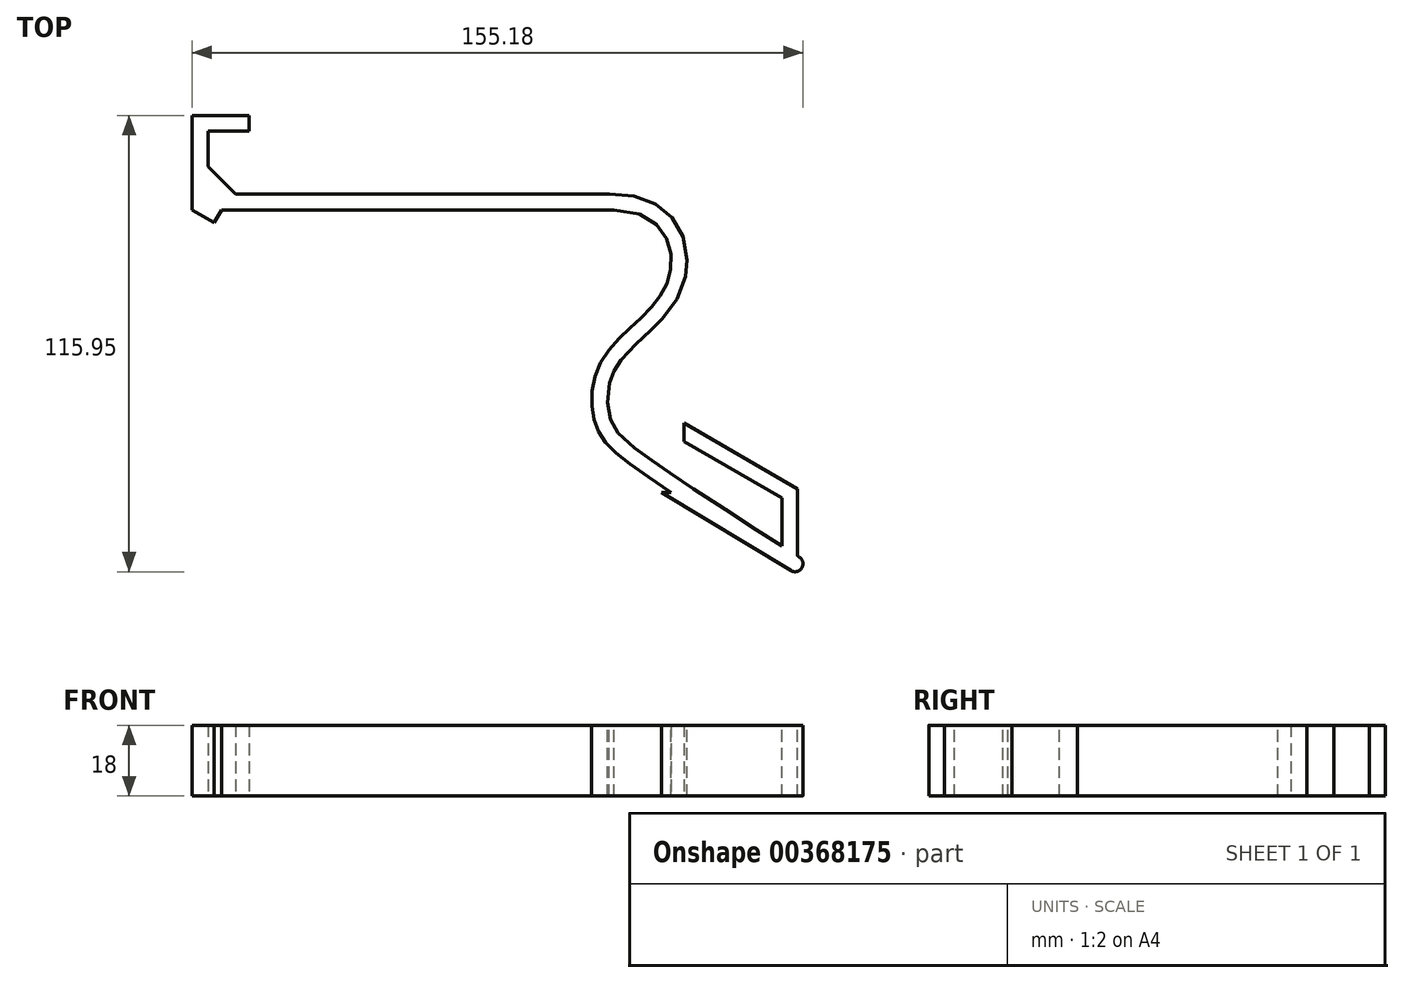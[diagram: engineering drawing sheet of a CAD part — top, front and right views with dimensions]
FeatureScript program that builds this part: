
annotation { "Feature Type Name" : "Feature", "Feature Type Description" : "" }
export const myFeature = defineFeature(function(context is Context, id is Id, definition is map)
    precondition{}
    {
        {
            var Q0;
            Q0=qCreatedBy(makeId("Top.planeOp"),FACE);
            var sketch = newSketch(context, id + "F0", { "sketchPlane" : qUnion([Q0])});
            skLineSegment(sketch, "E0", {"start": v(0, 16) * mm, "end": v(-10.43, 16) * mm});
            skLineSegment(sketch, "E1", {"start": v(-10.43, 16) * mm, "end": v(-10.43, 0) * mm});
            skLineSegment(sketch, "E2", {"start": v(-10.43, 0) * mm, "end": v(95.57, 0) * mm});
            skLineSegment(sketch, "E3.0", {"start": v(-14.43, -4) * mm, "end": v(95.57, -4) * mm});
            skLineSegment(sketch, "E3.1", {"start": v(-14.43, 20) * mm, "end": v(-14.43, -4) * mm});
            skLineSegment(sketch, "E3.2", {"start": v(0, 20) * mm, "end": v(-14.43, 20) * mm});
            skLineSegment(sketch, "E4", {"start": v(0, 16) * mm, "end": v(0, 20) * mm});
            skLineSegment(sketch, "E5", {"start": v(95.57, 0) * mm, "end": v(95.57, -4) * mm});
            skLineSegment(sketch, "E6", {"start": v(-10.43, 7) * mm, "end": v(-3.43, 0) * mm});
            skLineSegment(sketch, "E7", {"start": v(95.57, -4) * mm, "end": v(95.57, -70.27) * mm});
            skLineSegment(sketch, "E8", {"start": v(95.57, -70.27) * mm, "end": v(91.57, -67.86) * mm});
            skLineSegment(sketch, "E9", {"start": v(91.57, -67.86) * mm, "end": v(91.57, -4) * mm});
            skLineSegment(sketch, "E10", {"start": v(-14.43, -4) * mm, "end": v(95.57, -70.27) * mm, "construction": true});
            skSolve(sketch);
        }
        {
            var Q0;
            Q0=qSketchRegion(id+"F0",true);
            extrude(context, id + "F1", {"entities" : qUnion([Q0]), "depth" : 18 * mm, "symmetric" : true});
        }
        {
            var Q0;
            Q0=makeQuery(id+"F1.opExtrude","CAP_FACE",FACE,{"disambiguationData":[OSD([sQuery(id+"F0.wireOp",EDGE,"E0"),sQuery(id+"F0.wireOp",EDGE,"E1"),sQuery(id+"F0.wireOp",EDGE,"E2"),sQuery(id+"F0.wireOp",EDGE,"E3.0"),sQuery(id+"F0.wireOp",EDGE,"E3.1"),sQuery(id+"F0.wireOp",EDGE,"E3.2"),sQuery(id+"F0.wireOp",EDGE,"E4"),sQuery(id+"F0.wireOp",EDGE,"E5"),sQuery(id+"F0.wireOp",EDGE,"E6"),sQuery(id+"F0.wireOp",EDGE,"E7"),sQuery(id+"F0.wireOp",EDGE,"E8"),sQuery(id+"F0.wireOp",EDGE,"E9")])],"isStart":false});
            var sketch = newSketch(context, id + "F2", { "sketchPlane" : qUnion([Q0])});
            skLineSegment(sketch, "E11", {"start": v(95.57, -70.27) * mm, "end": v(-14.43, -4) * mm});
            skLineSegment(sketch, "E12", {"start": v(-14.43, -4) * mm, "end": v(-43.04, -4) * mm});
            skLineSegment(sketch, "E13", {"start": v(-43.04, -4) * mm, "end": v(-43.04, -70.27) * mm});
            skLineSegment(sketch, "E14", {"start": v(-43.04, -70.27) * mm, "end": v(95.57, -70.27) * mm});
            skSolve(sketch);
        }
        {
            var Q0;
            Q0=qSketchRegion(id+"F2",true);
            extrude(context, id + "F3", {"entities" : qUnion([Q0]), "operationType" : NewBodyOperationType.REMOVE, "oppositeDirection" : true, "depth" : 25 * mm});
        }
        {
            var Q0;
            Q0=makeQuery(id+"F1.opExtrude","CAP_FACE",FACE,{"disambiguationData":[OSD([sQuery(id+"F0.wireOp",EDGE,"E0"),sQuery(id+"F0.wireOp",EDGE,"E1"),sQuery(id+"F0.wireOp",EDGE,"E2"),sQuery(id+"F0.wireOp",EDGE,"E3.0"),sQuery(id+"F0.wireOp",EDGE,"E3.1"),sQuery(id+"F0.wireOp",EDGE,"E3.2"),sQuery(id+"F0.wireOp",EDGE,"E4"),sQuery(id+"F0.wireOp",EDGE,"E5"),sQuery(id+"F0.wireOp",EDGE,"E6"),sQuery(id+"F0.wireOp",EDGE,"E7"),sQuery(id+"F0.wireOp",EDGE,"E8"),sQuery(id+"F0.wireOp",EDGE,"E9")])],"isStart":false});
            var sketch = newSketch(context, id + "F4", { "sketchPlane" : qUnion([Q0])});
            skCircle(sketch, "E15.cCircle", {"center": v(91.57, -4) * mm, "radius": 63.86 * mm, "construction": true});
            skLineSegment(sketch, "E15.0", {"start": v(91.57, -67.86) * mm, "end": v(36.26, -35.93) * mm});
            skLineSegment(sketch, "E15.1", {"start": v(36.26, -35.93) * mm, "end": v(36.26, 27.93) * mm});
            skLineSegment(sketch, "E15.2", {"start": v(36.26, 27.93) * mm, "end": v(91.57, 59.86) * mm});
            skLineSegment(sketch, "E15.3", {"start": v(91.57, 59.86) * mm, "end": v(146.87, 27.93) * mm});
            skLineSegment(sketch, "E15.4", {"start": v(146.87, 27.93) * mm, "end": v(146.87, -35.93) * mm});
            skLineSegment(sketch, "E15.5", {"start": v(146.87, -35.93) * mm, "end": v(91.57, -67.86) * mm});
            skCircle(sketch, "E16.cCircle", {"center": v(91.57, -4) * mm, "radius": 59.86 * mm, "construction": true});
            skLineSegment(sketch, "E16.0", {"start": v(91.57, -63.86) * mm, "end": v(39.73, -33.93) * mm});
            skLineSegment(sketch, "E16.1", {"start": v(39.73, -33.93) * mm, "end": v(39.73, 25.93) * mm});
            skLineSegment(sketch, "E16.2", {"start": v(39.73, 25.93) * mm, "end": v(91.57, 55.86) * mm});
            skLineSegment(sketch, "E16.3", {"start": v(91.57, 55.86) * mm, "end": v(143.4, 25.93) * mm});
            skLineSegment(sketch, "E16.4", {"start": v(143.4, 25.93) * mm, "end": v(143.4, -33.93) * mm});
            skLineSegment(sketch, "E16.5", {"start": v(143.4, -33.93) * mm, "end": v(91.57, -63.86) * mm});
            skSolve(sketch);
        }
        {
            var Q0;
            Q0=qSketchRegion(id+"F4",true);
            extrude(context, id + "F5", {"entities" : qUnion([Q0]), "operationType" : NewBodyOperationType.ADD, "oppositeDirection" : true, "depth" : 18 * mm});
        }
        {
            var Q0;
            Q0=makeQuery(id+"F5.boolean.opBoolean","MERGE",FACE,{"derivedFrom":[makeQuery(id+"F1.opExtrude","CAP_FACE",FACE,{"disambiguationData":[OSD([sQuery(id+"F0.wireOp",EDGE,"E0"),sQuery(id+"F0.wireOp",EDGE,"E1"),sQuery(id+"F0.wireOp",EDGE,"E2"),sQuery(id+"F0.wireOp",EDGE,"E3.0"),sQuery(id+"F0.wireOp",EDGE,"E3.1"),sQuery(id+"F0.wireOp",EDGE,"E3.2"),sQuery(id+"F0.wireOp",EDGE,"E4"),sQuery(id+"F0.wireOp",EDGE,"E5"),sQuery(id+"F0.wireOp",EDGE,"E6"),sQuery(id+"F0.wireOp",EDGE,"E7"),sQuery(id+"F0.wireOp",EDGE,"E8"),sQuery(id+"F0.wireOp",EDGE,"E9")])],"isStart":false}),makeQuery(id+"F5.opExtrude","CAP_FACE",FACE,{"disambiguationData":[OSD([sQuery(id+"F4.wireOp",EDGE,"E15.0"),sQuery(id+"F4.wireOp",EDGE,"E15.1"),sQuery(id+"F4.wireOp",EDGE,"E15.2"),sQuery(id+"F4.wireOp",EDGE,"E15.3"),sQuery(id+"F4.wireOp",EDGE,"E15.4"),sQuery(id+"F4.wireOp",EDGE,"E15.5"),sQuery(id+"F4.wireOp",EDGE,"E16.0"),sQuery(id+"F4.wireOp",EDGE,"E16.1"),sQuery(id+"F4.wireOp",EDGE,"E16.2"),sQuery(id+"F4.wireOp",EDGE,"E16.3"),sQuery(id+"F4.wireOp",EDGE,"E16.4"),sQuery(id+"F4.wireOp",EDGE,"E16.5")])],"isStart":true})]});
            var sketch = newSketch(context, id + "F6", { "sketchPlane" : qUnion([Q0])});
            skCircle(sketch, "E17.cCircle", {"center": v(95.57, 0) * mm, "radius": 53.55 * mm, "construction": true});
            skLineSegment(sketch, "E17.0", {"start": v(95.57, -53.55) * mm, "end": v(49.2, -26.77) * mm});
            skLineSegment(sketch, "E17.1", {"start": v(49.2, -26.77) * mm, "end": v(49.2, 26.77) * mm});
            skLineSegment(sketch, "E17.2", {"start": v(49.2, 26.77) * mm, "end": v(95.57, 53.55) * mm});
            skLineSegment(sketch, "E17.3", {"start": v(95.57, 53.55) * mm, "end": v(141.94, 26.77) * mm});
            skLineSegment(sketch, "E17.4", {"start": v(141.94, 26.77) * mm, "end": v(141.94, -26.77) * mm});
            skLineSegment(sketch, "E17.5", {"start": v(141.94, -26.77) * mm, "end": v(95.57, -53.55) * mm});
            skCircle(sketch, "E18.cCircle", {"center": v(95.57, 0) * mm, "radius": 49.55 * mm, "construction": true});
            skLineSegment(sketch, "E18.0", {"start": v(95.57, -49.55) * mm, "end": v(52.66, -24.77) * mm});
            skLineSegment(sketch, "E18.1", {"start": v(52.66, -24.77) * mm, "end": v(52.66, 24.77) * mm});
            skLineSegment(sketch, "E18.2", {"start": v(52.66, 24.77) * mm, "end": v(95.57, 49.55) * mm});
            skLineSegment(sketch, "E18.3", {"start": v(95.57, 49.55) * mm, "end": v(138.48, 24.77) * mm});
            skLineSegment(sketch, "E18.4", {"start": v(138.48, 24.77) * mm, "end": v(138.48, -24.77) * mm});
            skLineSegment(sketch, "E18.5", {"start": v(138.48, -24.77) * mm, "end": v(95.57, -49.55) * mm});
            skSolve(sketch);
        }
        {
            var Q0;
            Q0=qSketchRegion(id+"F6",true);
            extrude(context, id + "F7", {"entities" : qUnion([Q0]), "operationType" : NewBodyOperationType.ADD, "oppositeDirection" : true, "depth" : 18 * mm});
        }
        {
            var Q0;
            Q0=makeQuery(id+"F1.opExtrude","SWEPT_EDGE",EDGE,{"disambiguationData":[OSD([sQuery(id+"F0.wireOp",EDGE,"E3.0"),sQuery(id+"F0.wireOp",EDGE,"E9")])]});
            chamfer(context, id + "F8", {"entities" : qUnion([Q0]), "width" : 8 * mm, "tangentPropagation" : true});
        }
        {
            var Q0;
            Q0=makeQuery(id+"F1.opExtrude","SWEPT_EDGE",EDGE,{"disambiguationData":[OSD([sQuery(id+"F0.wireOp",EDGE,"E2"),sQuery(id+"F0.wireOp",EDGE,"E5")])]});
            chamfer(context, id + "F9", {"entities" : qUnion([Q0]), "width" : 8 * mm, "tangentPropagation" : true});
        }
        {
            var Q0;
            Q0=makeQuery(id+"F7.boolean.opBoolean","MERGE",FACE,{"derivedFrom":[makeQuery(id+"F5.boolean.opBoolean","MERGE",FACE,{"derivedFrom":[makeQuery(id+"F1.opExtrude","CAP_FACE",FACE,{"disambiguationData":[OSD([sQuery(id+"F0.wireOp",EDGE,"E0"),sQuery(id+"F0.wireOp",EDGE,"E1"),sQuery(id+"F0.wireOp",EDGE,"E2"),sQuery(id+"F0.wireOp",EDGE,"E3.0"),sQuery(id+"F0.wireOp",EDGE,"E3.1"),sQuery(id+"F0.wireOp",EDGE,"E3.2"),sQuery(id+"F0.wireOp",EDGE,"E4"),sQuery(id+"F0.wireOp",EDGE,"E5"),sQuery(id+"F0.wireOp",EDGE,"E6"),sQuery(id+"F0.wireOp",EDGE,"E7"),sQuery(id+"F0.wireOp",EDGE,"E8"),sQuery(id+"F0.wireOp",EDGE,"E9")])],"isStart":false}),makeQuery(id+"F5.opExtrude","CAP_FACE",FACE,{"disambiguationData":[OSD([sQuery(id+"F4.wireOp",EDGE,"E15.0"),sQuery(id+"F4.wireOp",EDGE,"E15.1"),sQuery(id+"F4.wireOp",EDGE,"E15.2"),sQuery(id+"F4.wireOp",EDGE,"E15.3"),sQuery(id+"F4.wireOp",EDGE,"E15.4"),sQuery(id+"F4.wireOp",EDGE,"E15.5"),sQuery(id+"F4.wireOp",EDGE,"E16.0"),sQuery(id+"F4.wireOp",EDGE,"E16.1"),sQuery(id+"F4.wireOp",EDGE,"E16.2"),sQuery(id+"F4.wireOp",EDGE,"E16.3"),sQuery(id+"F4.wireOp",EDGE,"E16.4"),sQuery(id+"F4.wireOp",EDGE,"E16.5")])],"isStart":true})]}),makeQuery(id+"F7.opExtrude","CAP_FACE",FACE,{"disambiguationData":[OSD([sQuery(id+"F6.wireOp",EDGE,"E17.0"),sQuery(id+"F6.wireOp",EDGE,"E17.1"),sQuery(id+"F6.wireOp",EDGE,"E17.2"),sQuery(id+"F6.wireOp",EDGE,"E17.3"),sQuery(id+"F6.wireOp",EDGE,"E17.4"),sQuery(id+"F6.wireOp",EDGE,"E17.5"),sQuery(id+"F6.wireOp",EDGE,"E18.0"),sQuery(id+"F6.wireOp",EDGE,"E18.1"),sQuery(id+"F6.wireOp",EDGE,"E18.2"),sQuery(id+"F6.wireOp",EDGE,"E18.3"),sQuery(id+"F6.wireOp",EDGE,"E18.4"),sQuery(id+"F6.wireOp",EDGE,"E18.5")])],"isStart":true})]});
            var sketch = newSketch(context, id + "F10", { "sketchPlane" : qUnion([Q0])});
            skLineSegment(sketch, "E19", {"start": v(28.5, 0) * mm, "end": v(95.57, 0) * mm});
            skLineSegment(sketch, "E20", {"start": v(95.57, 0) * mm, "end": v(95.57, -73.17) * mm});
            skLineSegment(sketch, "E21", {"start": v(95.57, -73.17) * mm, "end": v(150.76, -38.64) * mm});
            skLineSegment(sketch, "E22", {"start": v(150.76, -38.64) * mm, "end": v(155.26, 64.33) * mm});
            skLineSegment(sketch, "E23", {"start": v(155.26, 64.33) * mm, "end": v(108.49, 79.65) * mm});
            skLineSegment(sketch, "E24", {"start": v(108.49, 79.65) * mm, "end": v(24.9, 40.95) * mm});
            skLineSegment(sketch, "E25", {"start": v(24.9, 40.95) * mm, "end": v(28.5, 0) * mm});
            skSolve(sketch);
        }
        {
            var Q0;
            Q0=qSketchRegion(id+"F10",true);
            extrude(context, id + "F11", {"entities" : qUnion([Q0]), "operationType" : NewBodyOperationType.REMOVE, "oppositeDirection" : true, "depth" : 25 * mm});
        }
        {
            var Q0;
            Q0=makeQuery(id+"F7.boolean.opBoolean","MERGE",FACE,{"derivedFrom":[makeQuery(id+"F5.boolean.opBoolean","MERGE",FACE,{"derivedFrom":[makeQuery(id+"F1.opExtrude","CAP_FACE",FACE,{"disambiguationData":[OSD([sQuery(id+"F0.wireOp",EDGE,"E0"),sQuery(id+"F0.wireOp",EDGE,"E1"),sQuery(id+"F0.wireOp",EDGE,"E2"),sQuery(id+"F0.wireOp",EDGE,"E3.0"),sQuery(id+"F0.wireOp",EDGE,"E3.1"),sQuery(id+"F0.wireOp",EDGE,"E3.2"),sQuery(id+"F0.wireOp",EDGE,"E4"),sQuery(id+"F0.wireOp",EDGE,"E5"),sQuery(id+"F0.wireOp",EDGE,"E6"),sQuery(id+"F0.wireOp",EDGE,"E7"),sQuery(id+"F0.wireOp",EDGE,"E8"),sQuery(id+"F0.wireOp",EDGE,"E9")])],"isStart":false}),makeQuery(id+"F5.opExtrude","CAP_FACE",FACE,{"disambiguationData":[OSD([sQuery(id+"F4.wireOp",EDGE,"E15.0"),sQuery(id+"F4.wireOp",EDGE,"E15.1"),sQuery(id+"F4.wireOp",EDGE,"E15.2"),sQuery(id+"F4.wireOp",EDGE,"E15.3"),sQuery(id+"F4.wireOp",EDGE,"E15.4"),sQuery(id+"F4.wireOp",EDGE,"E15.5"),sQuery(id+"F4.wireOp",EDGE,"E16.0"),sQuery(id+"F4.wireOp",EDGE,"E16.1"),sQuery(id+"F4.wireOp",EDGE,"E16.2"),sQuery(id+"F4.wireOp",EDGE,"E16.3"),sQuery(id+"F4.wireOp",EDGE,"E16.4"),sQuery(id+"F4.wireOp",EDGE,"E16.5")])],"isStart":true})]}),makeQuery(id+"F7.opExtrude","CAP_FACE",FACE,{"disambiguationData":[OSD([sQuery(id+"F6.wireOp",EDGE,"E17.0"),sQuery(id+"F6.wireOp",EDGE,"E17.1"),sQuery(id+"F6.wireOp",EDGE,"E17.2"),sQuery(id+"F6.wireOp",EDGE,"E17.3"),sQuery(id+"F6.wireOp",EDGE,"E17.4"),sQuery(id+"F6.wireOp",EDGE,"E17.5"),sQuery(id+"F6.wireOp",EDGE,"E18.0"),sQuery(id+"F6.wireOp",EDGE,"E18.1"),sQuery(id+"F6.wireOp",EDGE,"E18.2"),sQuery(id+"F6.wireOp",EDGE,"E18.3"),sQuery(id+"F6.wireOp",EDGE,"E18.4"),sQuery(id+"F6.wireOp",EDGE,"E18.5")])],"isStart":true})]});
            var sketch = newSketch(context, id + "F12", { "sketchPlane" : qUnion([Q0])});
            skLineSegment(sketch, "E26", {"start": v(-14.43, -4) * mm, "end": v(-8.84, -7.23) * mm});
            skLineSegment(sketch, "E27", {"start": v(-8.84, -7.23) * mm, "end": v(-6.97, -4) * mm});
            skLineSegment(sketch, "E28", {"start": v(-6.97, -4) * mm, "end": v(-14.43, -4) * mm});
            skSolve(sketch);
        }
        {
            var Q0;
            Q0=qSketchRegion(id+"F12",true);
            extrude(context, id + "F13", {"entities" : qUnion([Q0]), "operationType" : NewBodyOperationType.ADD, "oppositeDirection" : true, "depth" : 18 * mm});
        }
        {
            var Q0;
            Q0=makeQuery(id+"F13.boolean.opBoolean","MERGE",FACE,{"derivedFrom":[makeQuery(id+"F7.boolean.opBoolean","MERGE",FACE,{"derivedFrom":[makeQuery(id+"F5.boolean.opBoolean","MERGE",FACE,{"derivedFrom":[makeQuery(id+"F1.opExtrude","CAP_FACE",FACE,{"disambiguationData":[OSD([sQuery(id+"F0.wireOp",EDGE,"E0"),sQuery(id+"F0.wireOp",EDGE,"E1"),sQuery(id+"F0.wireOp",EDGE,"E2"),sQuery(id+"F0.wireOp",EDGE,"E3.0"),sQuery(id+"F0.wireOp",EDGE,"E3.1"),sQuery(id+"F0.wireOp",EDGE,"E3.2"),sQuery(id+"F0.wireOp",EDGE,"E4"),sQuery(id+"F0.wireOp",EDGE,"E5"),sQuery(id+"F0.wireOp",EDGE,"E6"),sQuery(id+"F0.wireOp",EDGE,"E7"),sQuery(id+"F0.wireOp",EDGE,"E8"),sQuery(id+"F0.wireOp",EDGE,"E9")])],"isStart":false}),makeQuery(id+"F5.opExtrude","CAP_FACE",FACE,{"disambiguationData":[OSD([sQuery(id+"F4.wireOp",EDGE,"E15.0"),sQuery(id+"F4.wireOp",EDGE,"E15.1"),sQuery(id+"F4.wireOp",EDGE,"E15.2"),sQuery(id+"F4.wireOp",EDGE,"E15.3"),sQuery(id+"F4.wireOp",EDGE,"E15.4"),sQuery(id+"F4.wireOp",EDGE,"E15.5"),sQuery(id+"F4.wireOp",EDGE,"E16.0"),sQuery(id+"F4.wireOp",EDGE,"E16.1"),sQuery(id+"F4.wireOp",EDGE,"E16.2"),sQuery(id+"F4.wireOp",EDGE,"E16.3"),sQuery(id+"F4.wireOp",EDGE,"E16.4"),sQuery(id+"F4.wireOp",EDGE,"E16.5")])],"isStart":true})]}),makeQuery(id+"F7.opExtrude","CAP_FACE",FACE,{"disambiguationData":[OSD([sQuery(id+"F6.wireOp",EDGE,"E17.0"),sQuery(id+"F6.wireOp",EDGE,"E17.1"),sQuery(id+"F6.wireOp",EDGE,"E17.2"),sQuery(id+"F6.wireOp",EDGE,"E17.3"),sQuery(id+"F6.wireOp",EDGE,"E17.4"),sQuery(id+"F6.wireOp",EDGE,"E17.5"),sQuery(id+"F6.wireOp",EDGE,"E18.0"),sQuery(id+"F6.wireOp",EDGE,"E18.1"),sQuery(id+"F6.wireOp",EDGE,"E18.2"),sQuery(id+"F6.wireOp",EDGE,"E18.3"),sQuery(id+"F6.wireOp",EDGE,"E18.4"),sQuery(id+"F6.wireOp",EDGE,"E18.5")])],"isStart":true})]}),makeQuery(id+"F13.opExtrude","CAP_FACE",FACE,{"disambiguationData":[OSD([sQuery(id+"F12.wireOp",EDGE,"E26"),sQuery(id+"F12.wireOp",EDGE,"E27"),sQuery(id+"F12.wireOp",EDGE,"E28")])],"isStart":true})]});
            var sketch = newSketch(context, id + "F14", { "sketchPlane" : qUnion([Q0])});
            skLineSegment(sketch, "E29", {"start": v(-14.43, -4) * mm, "end": v(95.57, -70.27) * mm});
            skLineSegment(sketch, "E30", {"start": v(95.57, -70.27) * mm, "end": v(95.57, -79.24) * mm});
            skLineSegment(sketch, "E31", {"start": v(95.57, -79.24) * mm, "end": v(-31.36, -4) * mm});
            skLineSegment(sketch, "E32", {"start": v(-31.36, -4) * mm, "end": v(-14.43, -4) * mm});
            skSolve(sketch);
        }
        {
            var Q0;
            Q0=qSketchRegion(id+"F14",true);
            extrude(context, id + "F15", {"entities" : qUnion([Q0]), "operationType" : NewBodyOperationType.REMOVE, "oppositeDirection" : true, "depth" : 25 * mm});
        }
        {
            var Q0;
            Q0=makeQuery(id+"F13.boolean.opBoolean","MERGE",FACE,{"derivedFrom":[makeQuery(id+"F7.boolean.opBoolean","MERGE",FACE,{"derivedFrom":[makeQuery(id+"F5.boolean.opBoolean","MERGE",FACE,{"derivedFrom":[makeQuery(id+"F1.opExtrude","CAP_FACE",FACE,{"disambiguationData":[OSD([sQuery(id+"F0.wireOp",EDGE,"E0"),sQuery(id+"F0.wireOp",EDGE,"E1"),sQuery(id+"F0.wireOp",EDGE,"E2"),sQuery(id+"F0.wireOp",EDGE,"E3.0"),sQuery(id+"F0.wireOp",EDGE,"E3.1"),sQuery(id+"F0.wireOp",EDGE,"E3.2"),sQuery(id+"F0.wireOp",EDGE,"E4"),sQuery(id+"F0.wireOp",EDGE,"E5"),sQuery(id+"F0.wireOp",EDGE,"E6"),sQuery(id+"F0.wireOp",EDGE,"E7"),sQuery(id+"F0.wireOp",EDGE,"E8"),sQuery(id+"F0.wireOp",EDGE,"E9")])],"isStart":false}),makeQuery(id+"F5.opExtrude","CAP_FACE",FACE,{"disambiguationData":[OSD([sQuery(id+"F4.wireOp",EDGE,"E15.0"),sQuery(id+"F4.wireOp",EDGE,"E15.1"),sQuery(id+"F4.wireOp",EDGE,"E15.2"),sQuery(id+"F4.wireOp",EDGE,"E15.3"),sQuery(id+"F4.wireOp",EDGE,"E15.4"),sQuery(id+"F4.wireOp",EDGE,"E15.5"),sQuery(id+"F4.wireOp",EDGE,"E16.0"),sQuery(id+"F4.wireOp",EDGE,"E16.1"),sQuery(id+"F4.wireOp",EDGE,"E16.2"),sQuery(id+"F4.wireOp",EDGE,"E16.3"),sQuery(id+"F4.wireOp",EDGE,"E16.4"),sQuery(id+"F4.wireOp",EDGE,"E16.5")])],"isStart":true})]}),makeQuery(id+"F7.opExtrude","CAP_FACE",FACE,{"disambiguationData":[OSD([sQuery(id+"F6.wireOp",EDGE,"E17.0"),sQuery(id+"F6.wireOp",EDGE,"E17.1"),sQuery(id+"F6.wireOp",EDGE,"E17.2"),sQuery(id+"F6.wireOp",EDGE,"E17.3"),sQuery(id+"F6.wireOp",EDGE,"E17.4"),sQuery(id+"F6.wireOp",EDGE,"E17.5"),sQuery(id+"F6.wireOp",EDGE,"E18.0"),sQuery(id+"F6.wireOp",EDGE,"E18.1"),sQuery(id+"F6.wireOp",EDGE,"E18.2"),sQuery(id+"F6.wireOp",EDGE,"E18.3"),sQuery(id+"F6.wireOp",EDGE,"E18.4"),sQuery(id+"F6.wireOp",EDGE,"E18.5")])],"isStart":true})]}),makeQuery(id+"F13.opExtrude","CAP_FACE",FACE,{"disambiguationData":[OSD([sQuery(id+"F12.wireOp",EDGE,"E26"),sQuery(id+"F12.wireOp",EDGE,"E27"),sQuery(id+"F12.wireOp",EDGE,"E28")])],"isStart":true})]});
            var sketch = newSketch(context, id + "F16", { "sketchPlane" : qUnion([Q0])});
            skLineSegment(sketch, "E33", {"start": v(91.57, -63.86) * mm, "end": v(39.73, -32.63) * mm});
            skLineSegment(sketch, "E34", {"start": v(39.73, -32.63) * mm, "end": v(36.26, -34.54) * mm});
            skLineSegment(sketch, "E35", {"start": v(36.26, -34.54) * mm, "end": v(91.57, -67.86) * mm});
            skLineSegment(sketch, "E36", {"start": v(91.57, -67.86) * mm, "end": v(91.57, -63.86) * mm});
            skSolve(sketch);
        }
        {
            var Q0;
            Q0=qSketchRegion(id+"F16",true);
            extrude(context, id + "F17", {"entities" : qUnion([Q0]), "operationType" : NewBodyOperationType.ADD, "oppositeDirection" : true, "depth" : 18 * mm});
        }
        {
            var Q0;
            Q0=makeQuery(id+"F17.boolean.opBoolean","MERGE",FACE,{"derivedFrom":[makeQuery(id+"F13.boolean.opBoolean","MERGE",FACE,{"derivedFrom":[makeQuery(id+"F7.boolean.opBoolean","MERGE",FACE,{"derivedFrom":[makeQuery(id+"F5.boolean.opBoolean","MERGE",FACE,{"derivedFrom":[makeQuery(id+"F1.opExtrude","CAP_FACE",FACE,{"disambiguationData":[OSD([sQuery(id+"F0.wireOp",EDGE,"E0"),sQuery(id+"F0.wireOp",EDGE,"E1"),sQuery(id+"F0.wireOp",EDGE,"E2"),sQuery(id+"F0.wireOp",EDGE,"E3.0"),sQuery(id+"F0.wireOp",EDGE,"E3.1"),sQuery(id+"F0.wireOp",EDGE,"E3.2"),sQuery(id+"F0.wireOp",EDGE,"E4"),sQuery(id+"F0.wireOp",EDGE,"E5"),sQuery(id+"F0.wireOp",EDGE,"E6"),sQuery(id+"F0.wireOp",EDGE,"E7"),sQuery(id+"F0.wireOp",EDGE,"E8"),sQuery(id+"F0.wireOp",EDGE,"E9")])],"isStart":false}),makeQuery(id+"F5.opExtrude","CAP_FACE",FACE,{"disambiguationData":[OSD([sQuery(id+"F4.wireOp",EDGE,"E15.0"),sQuery(id+"F4.wireOp",EDGE,"E15.1"),sQuery(id+"F4.wireOp",EDGE,"E15.2"),sQuery(id+"F4.wireOp",EDGE,"E15.3"),sQuery(id+"F4.wireOp",EDGE,"E15.4"),sQuery(id+"F4.wireOp",EDGE,"E15.5"),sQuery(id+"F4.wireOp",EDGE,"E16.0"),sQuery(id+"F4.wireOp",EDGE,"E16.1"),sQuery(id+"F4.wireOp",EDGE,"E16.2"),sQuery(id+"F4.wireOp",EDGE,"E16.3"),sQuery(id+"F4.wireOp",EDGE,"E16.4"),sQuery(id+"F4.wireOp",EDGE,"E16.5")])],"isStart":true})]}),makeQuery(id+"F7.opExtrude","CAP_FACE",FACE,{"disambiguationData":[OSD([sQuery(id+"F6.wireOp",EDGE,"E17.0"),sQuery(id+"F6.wireOp",EDGE,"E17.1"),sQuery(id+"F6.wireOp",EDGE,"E17.2"),sQuery(id+"F6.wireOp",EDGE,"E17.3"),sQuery(id+"F6.wireOp",EDGE,"E17.4"),sQuery(id+"F6.wireOp",EDGE,"E17.5"),sQuery(id+"F6.wireOp",EDGE,"E18.0"),sQuery(id+"F6.wireOp",EDGE,"E18.1"),sQuery(id+"F6.wireOp",EDGE,"E18.2"),sQuery(id+"F6.wireOp",EDGE,"E18.3"),sQuery(id+"F6.wireOp",EDGE,"E18.4"),sQuery(id+"F6.wireOp",EDGE,"E18.5")])],"isStart":true})]}),makeQuery(id+"F13.opExtrude","CAP_FACE",FACE,{"disambiguationData":[OSD([sQuery(id+"F12.wireOp",EDGE,"E26"),sQuery(id+"F12.wireOp",EDGE,"E27"),sQuery(id+"F12.wireOp",EDGE,"E28")])],"isStart":true})]}),makeQuery(id+"F17.opExtrude","CAP_FACE",FACE,{"disambiguationData":[OSD([sQuery(id+"F16.wireOp",EDGE,"E33"),sQuery(id+"F16.wireOp",EDGE,"E34"),sQuery(id+"F16.wireOp",EDGE,"E35"),sQuery(id+"F16.wireOp",EDGE,"E36")])],"isStart":true})]});
            var sketch = newSketch(context, id + "F18", { "sketchPlane" : qUnion([Q0])});
            skLineSegment(sketch, "E37", {"start": v(95.57, -70.27) * mm, "end": v(139.4, -96.68) * mm});
            skLineSegment(sketch, "E38", {"start": v(139.4, -96.68) * mm, "end": v(139.4, -92) * mm});
            skLineSegment(sketch, "E39", {"start": v(139.4, -92) * mm, "end": v(95.57, -65.6) * mm});
            skLineSegment(sketch, "E40", {"start": v(95.57, -65.6) * mm, "end": v(95.57, -8) * mm});
            skLineSegment(sketch, "E41", {"start": v(95.57, -8) * mm, "end": v(87.57, 0) * mm});
            skLineSegment(sketch, "E42", {"start": v(87.57, 0) * mm, "end": v(91.57, 0) * mm});
            skLineSegment(sketch, "E43", {"start": v(91.57, 0) * mm, "end": v(99.57, -8) * mm});
            skLineSegment(sketch, "E44", {"start": v(99.57, -8) * mm, "end": v(99.57, -68) * mm});
            skLineSegment(sketch, "E45", {"start": v(95.57, -70.27) * mm, "end": v(95.57, -65.6) * mm});
            skLineSegment(sketch, "E46", {"start": v(95.57, -49.55) * mm, "end": v(139.4, -74.86) * mm});
            skLineSegment(sketch, "E47", {"start": v(139.4, -74.86) * mm, "end": v(139.4, -79.48) * mm});
            skLineSegment(sketch, "E48", {"start": v(139.4, -79.48) * mm, "end": v(95.57, -54.17) * mm});
            skLineSegment(sketch, "E49", {"start": v(95.57, -54.17) * mm, "end": v(95.57, -49.55) * mm});
            skLineSegment(sketch, "E50", {"start": v(75.35, -37.88) * mm, "end": v(131.48, -70.28) * mm});
            skLineSegment(sketch, "E51", {"start": v(139.4, -92) * mm, "end": v(139.4, -79.48) * mm});
            skLineSegment(sketch, "E52", {"start": v(135.4, -89.6) * mm, "end": v(135.4, -77.17) * mm});
            skSolve(sketch);
        }
        {
            var Q0;
            Q0=qSketchRegion(id+"F18",true);
            extrude(context, id + "F19", {"entities" : qUnion([Q0]), "oppositeDirection" : true, "depth" : 18 * mm});
        }
        {
            var Q0;
            Q0=makeQuery(id+"F17.boolean.opBoolean","MERGE",FACE,{"derivedFrom":[makeQuery(id+"F13.boolean.opBoolean","MERGE",FACE,{"derivedFrom":[makeQuery(id+"F7.boolean.opBoolean","MERGE",FACE,{"derivedFrom":[makeQuery(id+"F5.boolean.opBoolean","MERGE",FACE,{"derivedFrom":[makeQuery(id+"F1.opExtrude","CAP_FACE",FACE,{"disambiguationData":[OSD([sQuery(id+"F0.wireOp",EDGE,"E0"),sQuery(id+"F0.wireOp",EDGE,"E1"),sQuery(id+"F0.wireOp",EDGE,"E2"),sQuery(id+"F0.wireOp",EDGE,"E3.0"),sQuery(id+"F0.wireOp",EDGE,"E3.1"),sQuery(id+"F0.wireOp",EDGE,"E3.2"),sQuery(id+"F0.wireOp",EDGE,"E4"),sQuery(id+"F0.wireOp",EDGE,"E5"),sQuery(id+"F0.wireOp",EDGE,"E6"),sQuery(id+"F0.wireOp",EDGE,"E7"),sQuery(id+"F0.wireOp",EDGE,"E8"),sQuery(id+"F0.wireOp",EDGE,"E9")])],"isStart":false}),makeQuery(id+"F5.opExtrude","CAP_FACE",FACE,{"disambiguationData":[OSD([sQuery(id+"F4.wireOp",EDGE,"E15.0"),sQuery(id+"F4.wireOp",EDGE,"E15.1"),sQuery(id+"F4.wireOp",EDGE,"E15.2"),sQuery(id+"F4.wireOp",EDGE,"E15.3"),sQuery(id+"F4.wireOp",EDGE,"E15.4"),sQuery(id+"F4.wireOp",EDGE,"E15.5"),sQuery(id+"F4.wireOp",EDGE,"E16.0"),sQuery(id+"F4.wireOp",EDGE,"E16.1"),sQuery(id+"F4.wireOp",EDGE,"E16.2"),sQuery(id+"F4.wireOp",EDGE,"E16.3"),sQuery(id+"F4.wireOp",EDGE,"E16.4"),sQuery(id+"F4.wireOp",EDGE,"E16.5")])],"isStart":true})]}),makeQuery(id+"F7.opExtrude","CAP_FACE",FACE,{"disambiguationData":[OSD([sQuery(id+"F6.wireOp",EDGE,"E17.0"),sQuery(id+"F6.wireOp",EDGE,"E17.1"),sQuery(id+"F6.wireOp",EDGE,"E17.2"),sQuery(id+"F6.wireOp",EDGE,"E17.3"),sQuery(id+"F6.wireOp",EDGE,"E17.4"),sQuery(id+"F6.wireOp",EDGE,"E17.5"),sQuery(id+"F6.wireOp",EDGE,"E18.0"),sQuery(id+"F6.wireOp",EDGE,"E18.1"),sQuery(id+"F6.wireOp",EDGE,"E18.2"),sQuery(id+"F6.wireOp",EDGE,"E18.3"),sQuery(id+"F6.wireOp",EDGE,"E18.4"),sQuery(id+"F6.wireOp",EDGE,"E18.5")])],"isStart":true})]}),makeQuery(id+"F13.opExtrude","CAP_FACE",FACE,{"disambiguationData":[OSD([sQuery(id+"F12.wireOp",EDGE,"E26"),sQuery(id+"F12.wireOp",EDGE,"E27"),sQuery(id+"F12.wireOp",EDGE,"E28")])],"isStart":true})]}),makeQuery(id+"F17.opExtrude","CAP_FACE",FACE,{"disambiguationData":[OSD([sQuery(id+"F16.wireOp",EDGE,"E33"),sQuery(id+"F16.wireOp",EDGE,"E34"),sQuery(id+"F16.wireOp",EDGE,"E35"),sQuery(id+"F16.wireOp",EDGE,"E36")])],"isStart":true})]});
            var sketch = newSketch(context, id + "F20", { "sketchPlane" : qUnion([Q0])});
            skLineSegment(sketch, "E53.bottom", {"start": v(23.1, -4) * mm, "end": v(110.54, -4) * mm});
            skLineSegment(sketch, "E53.top", {"start": v(23.1, -75.82) * mm, "end": v(110.54, -75.82) * mm});
            skLineSegment(sketch, "E53.left", {"start": v(23.1, -4) * mm, "end": v(23.1, -75.82) * mm});
            skLineSegment(sketch, "E53.right", {"start": v(110.54, -4) * mm, "end": v(110.54, -75.82) * mm});
            skSolve(sketch);
        }
        {
            var Q0;
            Q0 = qSketchRegion(id + "F20", true);
            extrude(context, id + "F21", {"entities" : qUnion([Q0]), "operationType" : NewBodyOperationType.REMOVE, "oppositeDirection" : true, "depth" : 25 * mm, "offsetDistance" : 25 * mm});
        }
        {
            var Q0;
            Q0=makeQuery(id+"F17.boolean.opBoolean","MERGE",FACE,{"derivedFrom":[makeQuery(id+"F13.boolean.opBoolean","MERGE",FACE,{"derivedFrom":[makeQuery(id+"F7.boolean.opBoolean","MERGE",FACE,{"derivedFrom":[makeQuery(id+"F5.boolean.opBoolean","MERGE",FACE,{"derivedFrom":[makeQuery(id+"F1.opExtrude","CAP_FACE",FACE,{"disambiguationData":[OSD([sQuery(id+"F0.wireOp",EDGE,"E0"),sQuery(id+"F0.wireOp",EDGE,"E1"),sQuery(id+"F0.wireOp",EDGE,"E2"),sQuery(id+"F0.wireOp",EDGE,"E3.0"),sQuery(id+"F0.wireOp",EDGE,"E3.1"),sQuery(id+"F0.wireOp",EDGE,"E3.2"),sQuery(id+"F0.wireOp",EDGE,"E4"),sQuery(id+"F0.wireOp",EDGE,"E5"),sQuery(id+"F0.wireOp",EDGE,"E6"),sQuery(id+"F0.wireOp",EDGE,"E7"),sQuery(id+"F0.wireOp",EDGE,"E8"),sQuery(id+"F0.wireOp",EDGE,"E9")])],"isStart":false}),makeQuery(id+"F5.opExtrude","CAP_FACE",FACE,{"disambiguationData":[OSD([sQuery(id+"F4.wireOp",EDGE,"E15.0"),sQuery(id+"F4.wireOp",EDGE,"E15.1"),sQuery(id+"F4.wireOp",EDGE,"E15.2"),sQuery(id+"F4.wireOp",EDGE,"E15.3"),sQuery(id+"F4.wireOp",EDGE,"E15.4"),sQuery(id+"F4.wireOp",EDGE,"E15.5"),sQuery(id+"F4.wireOp",EDGE,"E16.0"),sQuery(id+"F4.wireOp",EDGE,"E16.1"),sQuery(id+"F4.wireOp",EDGE,"E16.2"),sQuery(id+"F4.wireOp",EDGE,"E16.3"),sQuery(id+"F4.wireOp",EDGE,"E16.4"),sQuery(id+"F4.wireOp",EDGE,"E16.5")])],"isStart":true})]}),makeQuery(id+"F7.opExtrude","CAP_FACE",FACE,{"disambiguationData":[OSD([sQuery(id+"F6.wireOp",EDGE,"E17.0"),sQuery(id+"F6.wireOp",EDGE,"E17.1"),sQuery(id+"F6.wireOp",EDGE,"E17.2"),sQuery(id+"F6.wireOp",EDGE,"E17.3"),sQuery(id+"F6.wireOp",EDGE,"E17.4"),sQuery(id+"F6.wireOp",EDGE,"E17.5"),sQuery(id+"F6.wireOp",EDGE,"E18.0"),sQuery(id+"F6.wireOp",EDGE,"E18.1"),sQuery(id+"F6.wireOp",EDGE,"E18.2"),sQuery(id+"F6.wireOp",EDGE,"E18.3"),sQuery(id+"F6.wireOp",EDGE,"E18.4"),sQuery(id+"F6.wireOp",EDGE,"E18.5")])],"isStart":true})]}),makeQuery(id+"F13.opExtrude","CAP_FACE",FACE,{"disambiguationData":[OSD([sQuery(id+"F12.wireOp",EDGE,"E26"),sQuery(id+"F12.wireOp",EDGE,"E27"),sQuery(id+"F12.wireOp",EDGE,"E28")])],"isStart":true})]}),makeQuery(id+"F17.opExtrude","CAP_FACE",FACE,{"disambiguationData":[OSD([sQuery(id+"F16.wireOp",EDGE,"E33"),sQuery(id+"F16.wireOp",EDGE,"E34"),sQuery(id+"F16.wireOp",EDGE,"E35"),sQuery(id+"F16.wireOp",EDGE,"E36")])],"isStart":true})]});
            var sketch = newSketch(context, id + "F22", { "sketchPlane" : qUnion([Q0])});
            skLineSegment(sketch, "E54", {"start": v(-14.43, -4) * mm, "end": v(139.4, -96.68) * mm, "construction": true});
            skFitSpline(sketch, "E55", {"points": [v(91.57, -4) * mm, v(107.22, -18.25) * mm, v(100.16, -30.93) * mm, v(89.08, -43.29) * mm, v(87.96, -58.22) * mm, v(100.48, -71.22) * mm, v(138.73, -96.27) * mm, v(139.4, -96.68) * mm], "startDerivative": vector(240.78, 4.66) * mm, "endDerivative": vector(9.36, -5.8) * mm});
            skFitSpline(sketch, "E56.0", {"points": [v(91.49, 0) * mm, v(92.9, 0.03) * mm, v(94.92, -0.06) * mm, v(97.38, -0.44) * mm, v(99.12, -0.84) * mm, v(100.75, -1.37) * mm, v(102.28, -2.01) * mm, v(103.69, -2.77) * mm, v(104.98, -3.64) * mm, v(106.15, -4.6) * mm, v(107.19, -5.64) * mm, v(108.1, -6.75) * mm, v(108.88, -7.9) * mm, v(109.54, -9.1) * mm, v(110.26, -10.74) * mm, v(110.89, -12.8) * mm, v(111.2, -14.85) * mm, v(111.28, -16.45) * mm, v(111.28, -17.43) * mm, v(111.24, -18.2) * mm, v(111.18, -18.96) * mm, v(111.06, -19.89) * mm, v(110.86, -20.98) * mm, v(110.52, -22.39) * mm, v(109.95, -24.08) * mm, v(109.08, -25.97) * mm, v(108.06, -27.73) * mm, v(106.92, -29.37) * mm, v(105.69, -30.9) * mm, v(104.6, -32.1) * mm, v(103.71, -33.03) * mm, v(103.15, -33.6) * mm, v(102.7, -34.04) * mm, v(102.24, -34.48) * mm, v(101.67, -35.03) * mm, v(100.99, -35.66) * mm, v(100.08, -36.5) * mm, v(98.97, -37.53) * mm, v(97.7, -38.73) * mm, v(96.49, -39.93) * mm, v(95.38, -41.12) * mm, v(94.56, -42.11) * mm, v(93.96, -42.9) * mm, v(93.55, -43.5) * mm, v(93.24, -44) * mm, v(93, -44.4) * mm, v(92.84, -44.71) * mm, v(92.71, -44.96) * mm, v(92.62, -45.17) * mm, v(92.52, -45.38) * mm, v(92.4, -45.64) * mm, v(92.22, -46.07) * mm, v(92.02, -46.62) * mm, v(91.8, -47.3) * mm, v(91.6, -48) * mm, v(91.4, -48.94) * mm, v(91.2, -50.16) * mm, v(91.1, -51.63) * mm, v(91.1, -53.08) * mm, v(91.21, -54.48) * mm, v(91.4, -55.57) * mm, v(91.59, -56.4) * mm, v(91.75, -56.97) * mm, v(91.94, -57.51) * mm, v(92.14, -58.02) * mm, v(92.36, -58.5) * mm, v(92.7, -59.12) * mm, v(93.18, -59.89) * mm, v(93.92, -60.83) * mm, v(94.87, -61.83) * mm, v(96.06, -62.92) * mm, v(97.5, -64.11) * mm, v(98.94, -65.2) * mm, v(100.23, -66.14) * mm, v(101.26, -66.88) * mm, v(102.37, -67.66) * mm, v(103.55, -68.49) * mm, v(104.8, -69.35) * mm, v(106.1, -70.24) * mm, v(107.46, -71.16) * mm, v(109.33, -72.43) * mm, v(111.77, -74.06) * mm, v(114.8, -76.07) * mm, v(118.93, -78.8) * mm, v(123.06, -81.5) * mm, v(127.01, -84.05) * mm, v(129.83, -85.87) * mm, v(132.46, -87.56) * mm, v(134.84, -89.08) * mm, v(136.93, -90.41) * mm, v(138.68, -91.52) * mm, v(139.8, -92.23) * mm, v(140.4, -92.6) * mm, v(140.63, -92.74) * mm, v(140.75, -92.82) * mm, v(140.86, -92.89) * mm, v(140.98, -92.96) * mm, v(141.09, -93.02) * mm, v(141.18, -93.08) * mm, v(141.24, -93.12) * mm, v(141.3, -93.15) * mm, v(141.36, -93.18) * mm, v(141.42, -93.22) * mm, v(141.48, -93.26) * mm, v(141.51, -93.28) * mm]});
            skLineSegment(sketch, "E57", {"start": v(85.84, 0) * mm, "end": v(91.49, 0) * mm});
            skLineSegment(sketch, "E58", {"start": v(141.51, -93.28) * mm, "end": v(139.4, -96.68) * mm});
            skLineSegment(sketch, "E59", {"start": v(85.84, 0) * mm, "end": v(91.57, -4) * mm});
            skSolve(sketch);
        }
        {
            var Q0;
            Q0 = qSketchRegion(id + "F22", true);
            extrude(context, id + "F23", {"entities" : qUnion([Q0]), "operationType" : NewBodyOperationType.ADD, "oppositeDirection" : true, "depth" : 18 * mm, "offsetDistance" : 25 * mm});
        }
        {
            var Q0;
            Q0=makeQuery(id+"F23.boolean.opBoolean","MERGE",FACE,{"derivedFrom":[makeQuery(id+"F17.boolean.opBoolean","MERGE",FACE,{"derivedFrom":[makeQuery(id+"F13.boolean.opBoolean","MERGE",FACE,{"derivedFrom":[makeQuery(id+"F7.boolean.opBoolean","MERGE",FACE,{"derivedFrom":[makeQuery(id+"F5.boolean.opBoolean","MERGE",FACE,{"derivedFrom":[makeQuery(id+"F1.opExtrude","CAP_FACE",FACE,{"disambiguationData":[OSD([sQuery(id+"F0.wireOp",EDGE,"E0"),sQuery(id+"F0.wireOp",EDGE,"E1"),sQuery(id+"F0.wireOp",EDGE,"E2"),sQuery(id+"F0.wireOp",EDGE,"E3.0"),sQuery(id+"F0.wireOp",EDGE,"E3.1"),sQuery(id+"F0.wireOp",EDGE,"E3.2"),sQuery(id+"F0.wireOp",EDGE,"E4"),sQuery(id+"F0.wireOp",EDGE,"E5"),sQuery(id+"F0.wireOp",EDGE,"E6"),sQuery(id+"F0.wireOp",EDGE,"E7"),sQuery(id+"F0.wireOp",EDGE,"E8"),sQuery(id+"F0.wireOp",EDGE,"E9")])],"isStart":false}),makeQuery(id+"F5.opExtrude","CAP_FACE",FACE,{"disambiguationData":[OSD([sQuery(id+"F4.wireOp",EDGE,"E15.0"),sQuery(id+"F4.wireOp",EDGE,"E15.1"),sQuery(id+"F4.wireOp",EDGE,"E15.2"),sQuery(id+"F4.wireOp",EDGE,"E15.3"),sQuery(id+"F4.wireOp",EDGE,"E15.4"),sQuery(id+"F4.wireOp",EDGE,"E15.5"),sQuery(id+"F4.wireOp",EDGE,"E16.0"),sQuery(id+"F4.wireOp",EDGE,"E16.1"),sQuery(id+"F4.wireOp",EDGE,"E16.2"),sQuery(id+"F4.wireOp",EDGE,"E16.3"),sQuery(id+"F4.wireOp",EDGE,"E16.4"),sQuery(id+"F4.wireOp",EDGE,"E16.5")])],"isStart":true})]}),makeQuery(id+"F7.opExtrude","CAP_FACE",FACE,{"disambiguationData":[OSD([sQuery(id+"F6.wireOp",EDGE,"E17.0"),sQuery(id+"F6.wireOp",EDGE,"E17.1"),sQuery(id+"F6.wireOp",EDGE,"E17.2"),sQuery(id+"F6.wireOp",EDGE,"E17.3"),sQuery(id+"F6.wireOp",EDGE,"E17.4"),sQuery(id+"F6.wireOp",EDGE,"E17.5"),sQuery(id+"F6.wireOp",EDGE,"E18.0"),sQuery(id+"F6.wireOp",EDGE,"E18.1"),sQuery(id+"F6.wireOp",EDGE,"E18.2"),sQuery(id+"F6.wireOp",EDGE,"E18.3"),sQuery(id+"F6.wireOp",EDGE,"E18.4"),sQuery(id+"F6.wireOp",EDGE,"E18.5")])],"isStart":true})]}),makeQuery(id+"F13.opExtrude","CAP_FACE",FACE,{"disambiguationData":[OSD([sQuery(id+"F12.wireOp",EDGE,"E26"),sQuery(id+"F12.wireOp",EDGE,"E27"),sQuery(id+"F12.wireOp",EDGE,"E28")])],"isStart":true})]}),makeQuery(id+"F17.opExtrude","CAP_FACE",FACE,{"disambiguationData":[OSD([sQuery(id+"F16.wireOp",EDGE,"E33"),sQuery(id+"F16.wireOp",EDGE,"E34"),sQuery(id+"F16.wireOp",EDGE,"E35"),sQuery(id+"F16.wireOp",EDGE,"E36")])],"isStart":true})]}),makeQuery(id+"F23.opExtrude","CAP_FACE",FACE,{"disambiguationData":[OSD([sQuery(id+"F22.wireOp",EDGE,"E55"),sQuery(id+"F22.wireOp",EDGE,"E56.0"),sQuery(id+"F22.wireOp",EDGE,"E57"),sQuery(id+"F22.wireOp",EDGE,"E58"),sQuery(id+"F22.wireOp",EDGE,"E59")])],"isStart":true})]});
            var sketch = newSketch(context, id + "F24", { "sketchPlane" : qUnion([Q0])});
            skCircle(sketch, "E60", {"center": v(94.12, -16.27) * mm, "radius": 15.74 * mm});
            skSolve(sketch);
        }
        {
            var Q0;
            Q0=makeQuery(id+"F23.opExtrude","SWEPT_EDGE",EDGE,{"disambiguationData":[OSD([sQuery(id+"F22.wireOp",EDGE,"E55"),sQuery(id+"F22.wireOp",EDGE,"E58")])]});
            var Q1;
            Q1=makeQuery(id+"F23.opExtrude","SWEPT_EDGE",EDGE,{"disambiguationData":[OSD([sQuery(id+"F22.wireOp",EDGE,"E56.0"),sQuery(id+"F22.wireOp",EDGE,"E58")])]});
            fillet(context, id + "F25", {"entities" : qUnion([Q0, Q1]), "tangentPropagation" : true, "radius" : 2 * mm, "defaultsChanged" : true, "vertexSettings" : [], "allowEdgeOverflow" : false});
        }
    });
